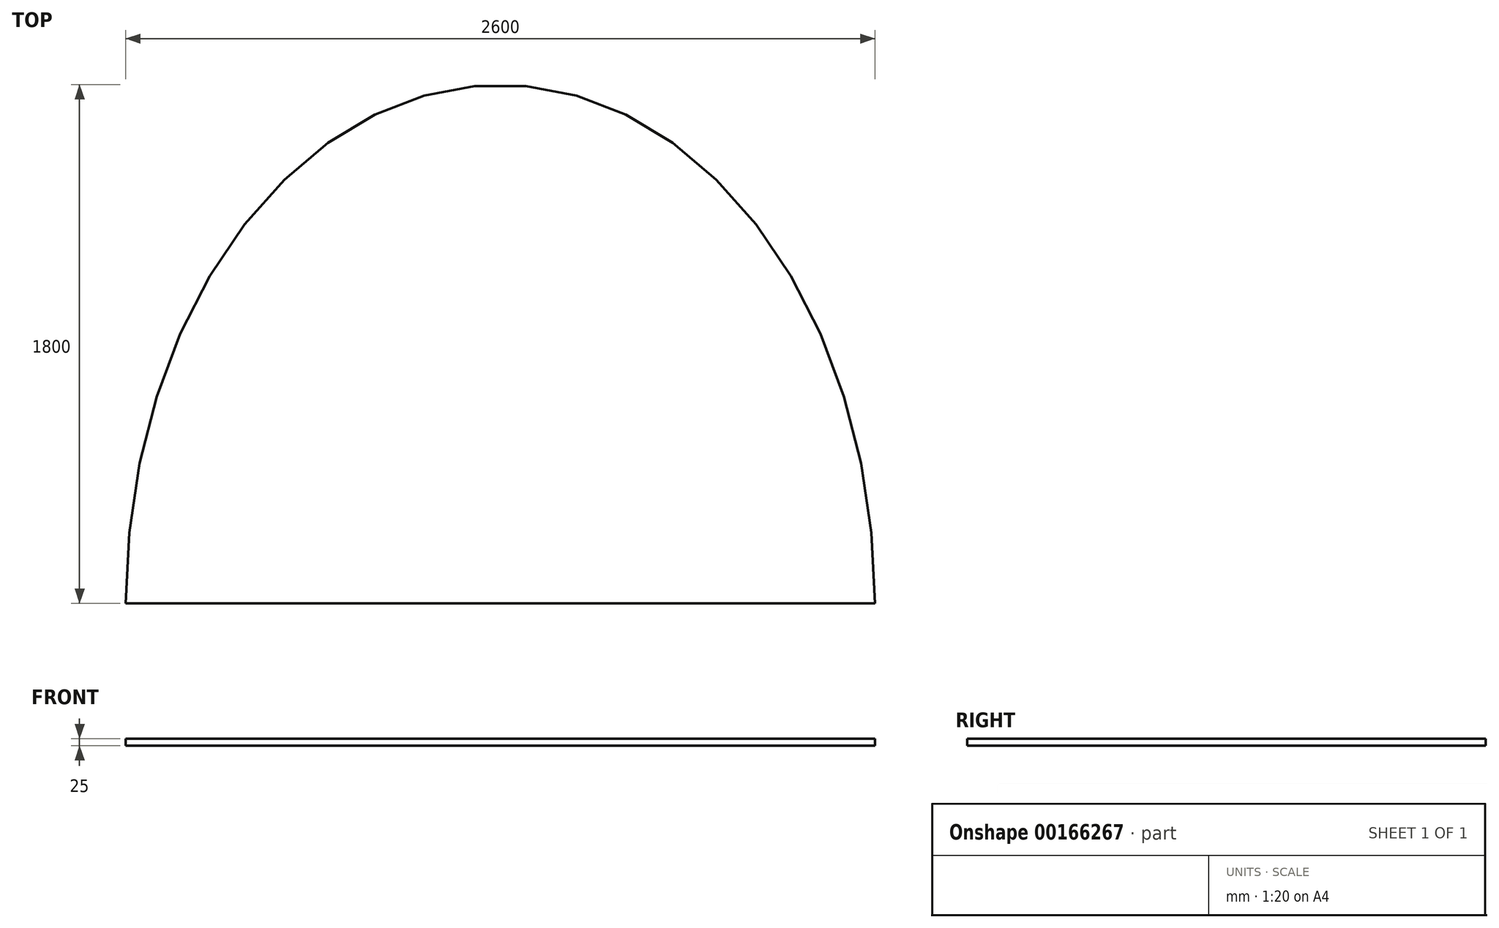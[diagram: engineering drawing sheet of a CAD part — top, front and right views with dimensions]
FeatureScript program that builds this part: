
annotation { "Feature Type Name" : "Feature", "Feature Type Description" : "" }
export const myFeature = defineFeature(function(context is Context, id is Id, definition is map)
    precondition{}
    {
        {
            var Q0;
            Q0=qCreatedBy(makeId("Top.planeOp"),FACE);
            var sketch = newSketch(context, id + "F0", { "sketchPlane" : qUnion([Q0])});
            skLineSegment(sketch, "E0", {"start": v(-1759.67, 1800) * mm, "end": v(1817.4, 1800) * mm, "construction": true});
            skLineSegment(sketch, "E1", {"start": v(-1300, 1800) * mm, "end": v(-1300, -243.02) * mm, "construction": true});
            skLineSegment(sketch, "E2", {"start": v(1300, 1800) * mm, "end": v(1300, -171.47) * mm, "construction": true});
            skLineSegment(sketch, "E3", {"start": v(-1534.75, 0) * mm, "end": v(1754.9, 0) * mm, "construction": true});
            skEllipticalArc(sketch, "E4", {});
            skLineSegment(sketch, "E5", {"start": v(-1300, 0) * mm, "end": v(1300, 0) * mm});
            const initialGuessF0  = {"E4": [0, 0, 1, 0, 1.3, 1.8, 6.283185307179586, 3.141592653589793]};
            skSetInitialGuess(sketch, initialGuessF0);
            skSolve(sketch);
        }
        {
            var Q0;
            Q0=makeQuery(id+"F0.imprint","IMPRINT",FACE,{"disambiguationData":[TD([[makeQuery(id+"F0.imprint","IMPRINT",EDGE,{"derivedFrom":sQuery(id+"F0.wireOp",EDGE,"E4")}),1.0]])]});
            extrude(context, id + "F1", {"entities" : qUnion([Q0]), "depth" : 25 * mm});
        }
    });
